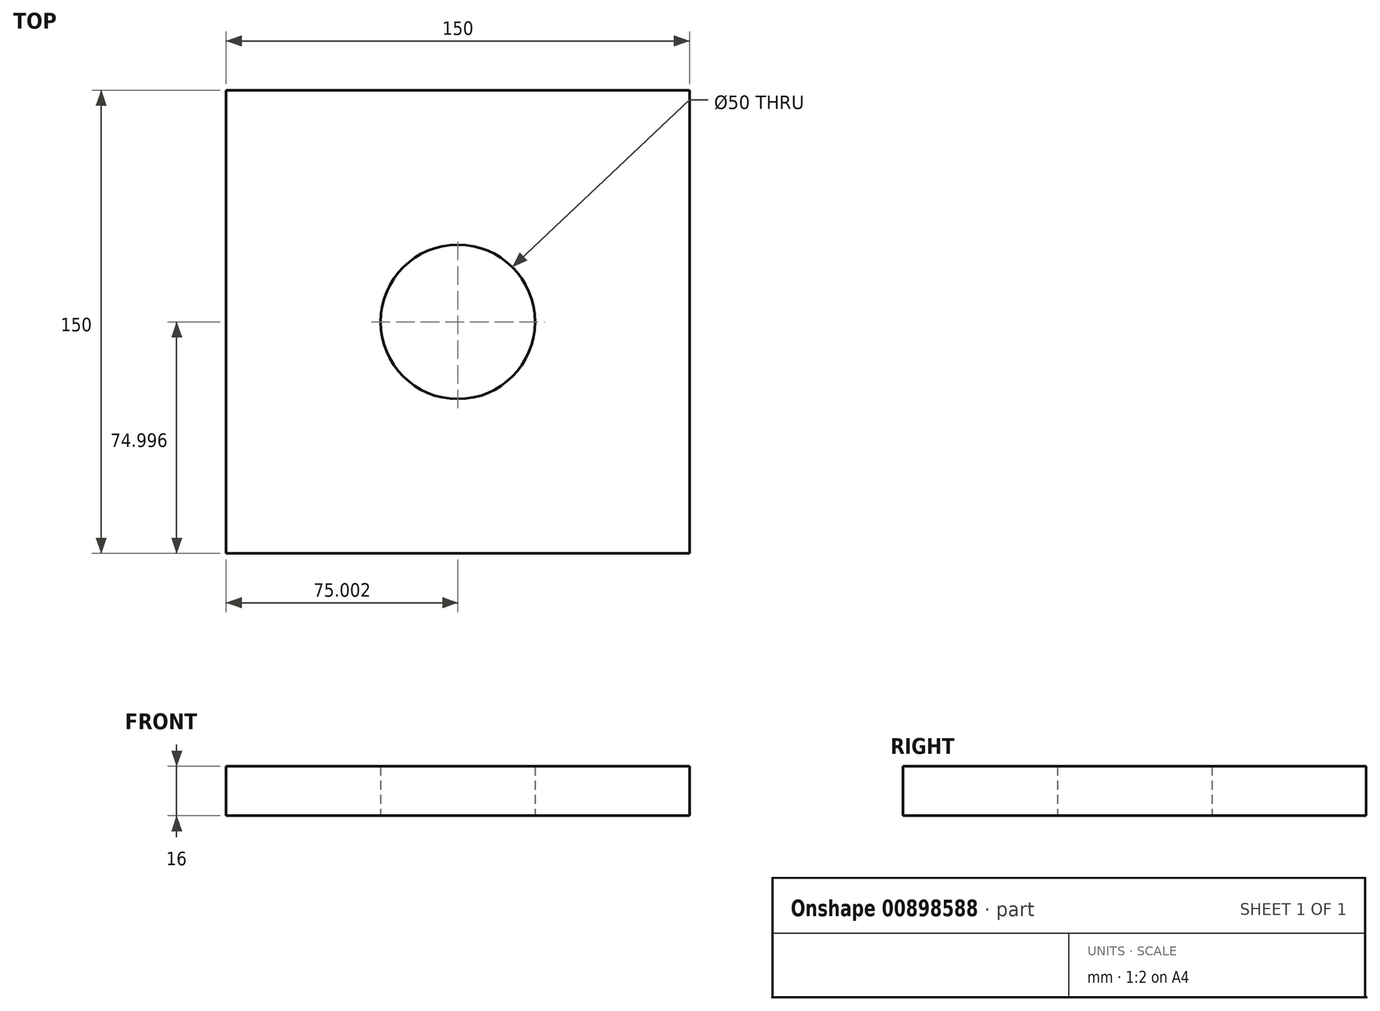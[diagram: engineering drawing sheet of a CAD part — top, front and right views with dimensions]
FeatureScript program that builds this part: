
annotation { "Feature Type Name" : "Feature", "Feature Type Description" : "" }
export const myFeature = defineFeature(function(context is Context, id is Id, definition is map)
    precondition{}
    {
        {
            var Q0;
            Q0=qCreatedBy(makeId("Top.planeOp"),FACE);
            var sketch = newSketch(context, id + "F0", { "sketchPlane" : qUnion([Q0])});
            skLineSegment(sketch, "E0.bottom", {"start": v(-127.1, 126.85) * mm, "end": v(22.9, 126.85) * mm});
            skLineSegment(sketch, "E0.top", {"start": v(-127.1, -23.15) * mm, "end": v(22.9, -23.15) * mm});
            skLineSegment(sketch, "E0.left", {"start": v(-127.1, 126.85) * mm, "end": v(-127.1, -23.15) * mm});
            skLineSegment(sketch, "E0.right", {"start": v(22.9, 126.85) * mm, "end": v(22.9, -23.15) * mm});
            skLineSegment(sketch, "E1", {"start": v(-127.1, 126.85) * mm, "end": v(22.9, -23.15) * mm, "construction": true});
            skCircle(sketch, "E2", {"center": v(-52.1, 51.85) * mm, "radius": 25 * mm});
            skSolve(sketch);
        }
        {
            var Q0;
            Q0 = qSketchRegion(id + "F0", true);
            var Q1;
            Q1=makeQuery(id+"F0.imprint","IMPRINT",FACE,{"disambiguationData":[TD([[makeQuery(id+"F0.imprint","IMPRINT",EDGE,{"derivedFrom":sQuery(id+"F0.wireOp",EDGE,"E0.bottom")}),-1.0]])]});
            extrude(context, id + "F1", {"entities" : qUnion([Q0, Q1]), "depth" : 16 * mm, "offsetDistance" : 25 * mm});
        }
    });
